# Revit family: 71_98_0502+0512_NESTED
name_source: partatom
category: Communication Devices
revit_build: Autodesk Revit 2015 (Build: 20141119_1515(x64)
units: mm (PartAtom-declared; Revit-internal decimal feet)

## types (6) — shared parameters
Basisplaat = Basisplaat
Breedte = 80 mm  [stored 0.262467 ft]
Consumption = 4 W
Default Elevation = 1219 mm
Diepte = 70 mm  [stored 0.229659 ft]
Dynamic range = > 90 dB
Frequency response = 200-20,000 Hz
Jack = Jack
Kabel = Kabel
Knoppen = Basisplaat
Lengte = 210 mm
Load impedance = 8 Ω
Manufacturer = Televic Conference
Maximum output power = > 1 W
Onderplaat = Inox
Scherm = Jack
Schroef = Basisplaat
Speaker = Jack
THD @ nominal level = < 0.1%
URL = http://www.televic-conference.com
Voltage = 48 V
Weight = 740

## per-type parameters (varying)
| type | Flexible microphone - 71.03.3540 | Microphone - 71.03.3140 | Model | Product ID | Type 71.98.0512 | Type Comments |
| Type 71.98.0502 - flexible microphone | Yes | No | Confidea F-DV | 71.98.0502 | No | Confidea Flushmount Delegate Voting Unit |
| Type 71.98.0502 - microphone | No | Yes | Confidea F-DV | 71.98.0502 | No | Confidea Flushmount Delegate Voting Unit
Description
The Confidea F-DV is Televic’s delegate panel for basic discussion systems, with an integrated speaker and electronic voting. Its small form factor, housed in an elegant casing, permits a minimalistic integration into any meeting room furniture. The integrated speaker creates a distributed sound field in the meeting room, increasing intelligibility without the need for an additional room sound system. The panel has a screw-lock connector to fit a removable microphone (available in 30, 40 or 50 cm versions). A 3.5 mm jack socket is available to connect headphones or a hearing loop for the hearing impaired. The voting systems includes 5 voting buttons and an RFID card reader for identification and authentication. The chairman version of this panel has additional controls (see Confidea F-CV 71.98.0512).
Benefits
The |
| Type 71.98.0502 - no microphone | No | No | Confidea F-DV | 71.98.0502 | No | Confidea Flushmount Delegate Voting Unit
Description
The Confidea F-DV is Televic’s delegate panel for basic discussion systems, with an integrated speaker and electronic voting. Its small form factor, housed in an elegant casing, permits a minimalistic integration into any meeting room furniture. The integrated speaker creates a distributed sound field in the meeting room, increasing intelligibility without the need for an additional room sound system. The panel has a screw-lock connector to fit a removable microphone (available in 30, 40 or 50 cm versions). A 3.5 mm jack socket is available to connect headphones or a hearing loop for the hearing impaired. The voting systems includes 5 voting buttons and an RFID card reader for identification and authentication. The chairman version of this panel has additional controls (see Confidea F-CV 71.98.0512).
Benefits
The |
| Type 71.98.0512 - flexible microphone | Yes | No | Confidea F-CV | 71.98.0512 | Yes | Confidea Flushmount Chairman Voting Unit |
| Type 71.98.0512 - microphone | No | Yes | Confidea F-CV | 71.98.0512 | Yes | Confidea Flushmount Chairman Voting Unit
Description
The Confidea F-CV is Televic’s chairman panel for basic discussion systems, with an integrated speaker and electronic voting. Its small form factor, housed in an elegant casing, permits a minimalistic integration into any meeting room furniture. The integrated speaker creates a distributed sound field in the meeting room, increasing intelligibility without the need for an additional room sound system. The panel has a screw-lock connector to fit a removable microphone (available in 30, 40 or 50 cm versions). A 3.5 mm jack socket is available to connect headphones or a hearing loop for the hearing impaired. |
| Type 71.98.0512 - no microphone | No | No | Confidea F-CV | 71.98.0512 | Yes | Confidea Flushmount Chairman Voting Unit
Description
The Confidea F-CV is Televic’s chairman panel for basic discussion systems, with an integrated speaker and electronic voting. Its small form factor, housed in an elegant casing, permits a minimalistic integration into any meeting room furniture. The integrated speaker creates a distributed sound field in the meeting room, increasing intelligibility without the need for an additional room sound system. The panel has a screw-lock connector to fit a removable microphone (available in 30, 40 or 50 cm versions). A 3.5 mm jack socket is available to connect headphones or a hearing loop for the hearing impaired. |

note: [stored X ft] marks values corroborated as IEEE doubles in the binary element streams (Revit-internal decimal feet)

## geometry (parser evidence)
native form markers: Sweep x13
no freeform markers — native parametric forms only
